# Revit family: Faucet-Lavatory-KOHLER-VITEO-K-16098A_1
name_source: partatom
category: Plumbing Fixtures
revit_build: Autodesk Revit 2017 (Build: 20160225_1515(x64)
units: mm (PartAtom-declared; Revit-internal decimal feet)

## family parameters
Cut with Voids When Loaded = No
Host = Face
OmniClass Number = 23.31.11.00
Part Type = Normal
Room Calculation Point = No
Round Connector Dimension = Use Diameter
Shared = No

## types (2) — shared parameters
ADA Compliant = No
Assembly Code = D2010
CW Connection = Yes
Cold Water Inlet = Cold Water Inlet
Date Modified = 08/29/2020
Default Elevation = 36"
Drain Included = No
Finish = Kohler-Metal-CP-Polished_Chrome
Flow Rate = 2 GPM
HW Connection = Yes
Handle Clearance = 3 11/16"
Hot Water Inlet = Hot Water Inlet
Length = 4 1/4"
Manufacturer = KOHLER Co.
Master Format 2014 = 22 41 39
Master Format 2014 Name = Residential Faucets, Supplies, and Trim
Material = Premium Metal Construction
Pressure = 116.00 psi
Product Name = VITEO
Spout Reach = 4 1/4"
URL = https://www.kohlerasiapacific.com
Vent Connection = No
Waste Connection = No
Waste Water Outlet = Waste Water Outlet
WaterSense Certified = No
Width = 1 7/8"

## per-type parameters (varying)
| type | 4ND | B4ND | Description | Height | Model | Spout Height | Type |
| 4ND, CP-Polished Chrome | Yes | No | Lever Basin Mixer | 4 15/16" | K-16098A-4ND-CP | 2" | 1 |
| B4ND, CP-Polished Chrome | No | Yes | Plus Basin Mixer | 5 3/4" | K-16098A-B4ND-CP | 2 13/16" | 2 |

## geometry (parser evidence)
native form markers: Sweep x5
no freeform markers — native parametric forms only
